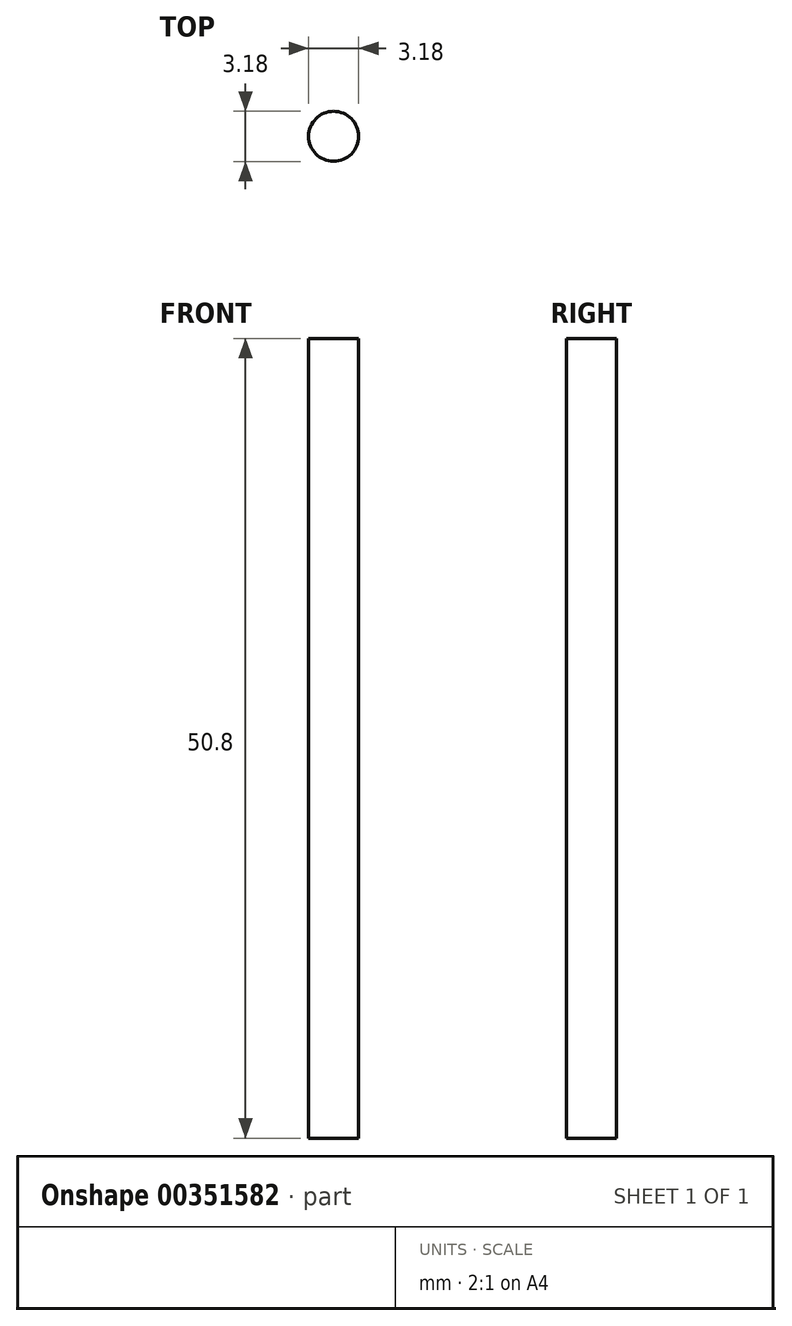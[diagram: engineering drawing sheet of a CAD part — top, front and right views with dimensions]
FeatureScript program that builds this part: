
annotation { "Feature Type Name" : "Feature", "Feature Type Description" : "" }
export const myFeature = defineFeature(function(context is Context, id is Id, definition is map)
    precondition{}
    {
        {
            var Q0;
            Q0=qCreatedBy(makeId("Top.planeOp"),FACE);
            var sketch = newSketch(context, id + "F0", { "sketchPlane" : qUnion([Q0])});
            skCircle(sketch, "E0", {"center": v(0, 0) * mm, "radius": 1.59 * mm});
            skSolve(sketch);
        }
        {
            var Q0;
            Q0 = qSketchRegion(id + "F0", true);
            extrude(context, id + "F1", {"entities" : qUnion([Q0]), "depth" : 50.8 * mm, "symmetric" : true});
        }
    });
